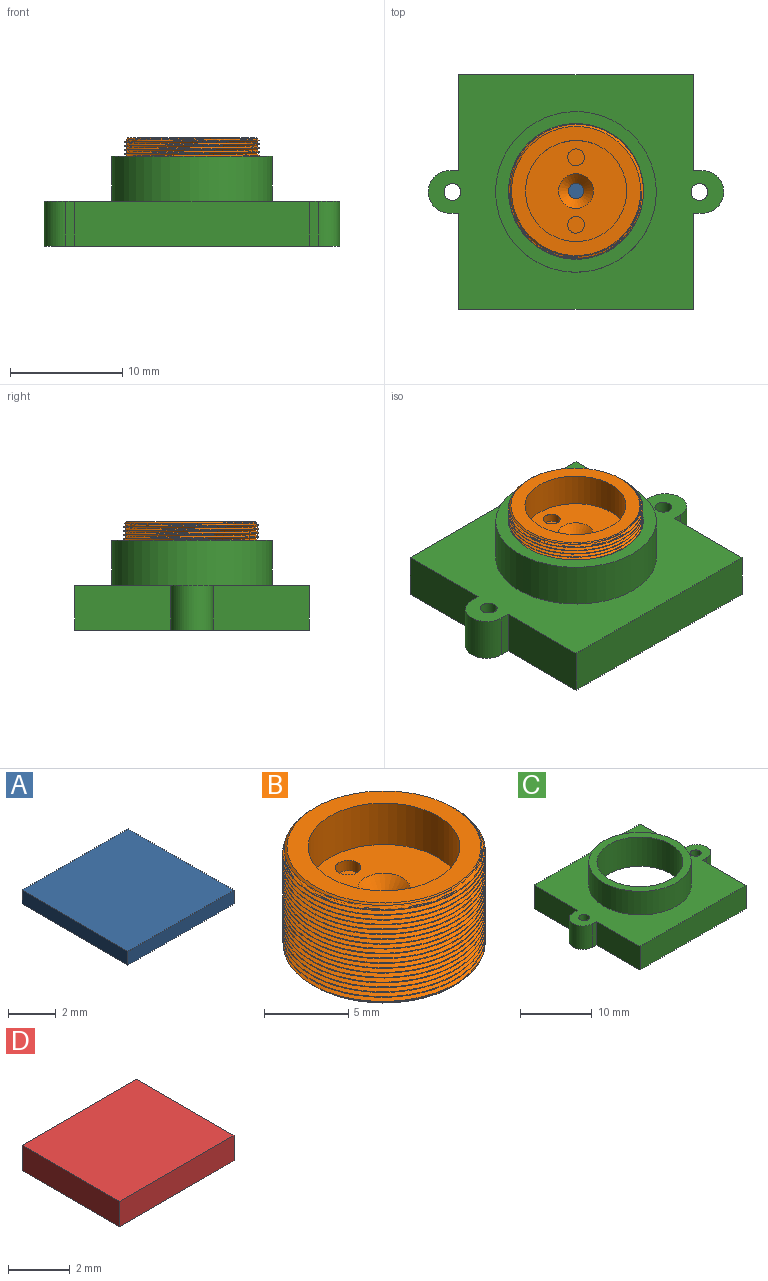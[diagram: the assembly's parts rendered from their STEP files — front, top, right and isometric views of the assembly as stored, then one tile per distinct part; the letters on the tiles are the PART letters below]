
ASSEMBLY  parts=4 mates=2
PART A: 6 faces, bbox 6.3x6.3x0.7 mm
  f0: plane 6.25x0.7mm, normal (0,-1,0), area 4.4mm2, adj f1,f3,f4,f5
  f1: plane 6.25x0.7mm, normal (1,0,0), area 4.4mm2, adj f0,f2,f4,f5
  f2: plane 6.25x0.7mm, normal (0,1,0), area 4.4mm2, adj f1,f3,f4,f5
  f3: plane 6.25x0.7mm, normal (-1,0,0), area 4.4mm2, adj f0,f2,f4,f5
  f4: plane 6.25x6.25mm, normal (0,0,1), area 39.1mm2, adj f0,f1,f2,f3
  f5: plane 6.25x6.25mm, normal (0,0,-1), area 39.1mm2, adj f0,f1,f2,f3
PART B: 21 faces, bbox 12x13.9x7.5 mm
  f0: plane 9x9mm, normal (0,0,1), area 52.5mm2, adj f2,f10,f17,f19
  f1: cylinder r=6mm len=12mm, axis (0,0,-1), area 27.8mm2, adj f11,f12,f15,f16
  f2: cylinder r=4.5mm len=9mm, axis (0,0,-1), area 84.8mm2, adj f0,f3
  f3: plane 11.5x11.5mm, normal (0,0,1), area 40.3mm2, adj f2,f13
  f4: cylinder r=4.5mm len=9mm, axis (0,0,1), area 35.3mm2, adj f5,f8
  f5: plane 11.5x11.5mm, normal (0,0,-1), area 40.2mm2, adj f4,f11,f15,f16
  f6: plane 6x6mm, normal (0,0,-1), area 26.8mm2, adj f7,f9
  f7: cylinder r=3mm len=6mm, axis (0,0,1), area 37.8mm2, adj f6,f8
  f8: plane 9x9mm, normal (0,0,-1), area 35.3mm2, adj f4,f7
  f9: cylinder r=0.69mm len=1.38mm, axis (0,0,1), area 0.6mm2, adj f6,f10
  f10: cone r=0.69mm half-angle=45deg, axis (0,0,1), area 8.6mm2, adj f0,f9
  f11: cone r=6mm half-angle=45deg, axis (0,0,1), area 7.2mm2, adj f1,f5,f15,f16
  f12: cone r=5.75mm half-angle=45deg, axis (0,0,-1), area 0.8mm2, adj f1,f13,f15,f16
  f13: cone r=5.75mm half-angle=45deg, axis (0,0,-1), area 6.7mm2, adj f3,f12,f14,f15
  f14: plane 0.11x0.08mm, normal (0,-1,0), area 0mm2, adj f13,f15,f16
  f15: bspline ~11.97x11.97mm, area 222.2mm2, adj f1,f5,f11,f12,f13,f14,f16
  f16: bspline ~13.86x12mm, area 220.7mm2, adj f1,f5,f11,f12,f14,f15
  f17: cylinder r=0.75mm len=1.5mm, axis (0,0,1), area 3.5mm2, adj f0,f18
  f18: plane 1.5x1.5mm, normal (0,0,1), area 1.8mm2, adj f17
  f19: cylinder r=0.75mm len=1.5mm, axis (0,0,1), area 3.5mm2, adj f0,f20
  f20: plane 1.5x1.5mm, normal (0,0,1), area 1.8mm2, adj f19
PART C: 24 faces, bbox 26.3x20.9x8 mm
  f0: plane 26.3x20.9mm, normal (0,0,-1), area 89.7mm2, adj f2,f3,f4,f5,f6,f7,f8,f9
  f1: cylinder r=6mm len=12mm, axis (0,0,1), area 188.5mm2, adj f18,f23
  f2: plane 8.55x4mm, normal (-1,0,0), area 34.2mm2, adj f0,f3,f14,f16
  f3: plane 20.9x4mm, normal (0,-1,0), area 83.6mm2, adj f0,f2,f4,f16
  f4: plane 8.55x4mm, normal (1,0,0), area 34.2mm2, adj f0,f3,f5,f16
  f5: plane 4x0.8mm, normal (0,-1,0), area 3.2mm2, adj f0,f4,f6,f16
  f6: cylinder r=1.9mm len=4mm, axis (0,0,-1), area 24mm2, adj f0,f5,f7,f16
  f7: plane 4x0.77mm, normal (-0.02,1,0), area 3.1mm2, adj f0,f6,f8,f16
  f8: plane 8.56x4mm, normal (1,0,0), area 34.3mm2, adj f0,f7,f9,f16
  f9: plane 20.9x4mm, normal (0,1,0), area 83.6mm2, adj f0,f8,f10,f16
  f10: plane 8.56x4mm, normal (-1,0,0), area 34.3mm2, adj f0,f9,f11,f16
  f11: plane 4x0.77mm, normal (0.02,1,0), area 3.1mm2, adj f0,f10,f12,f16
  f12: cylinder r=1.9mm len=4mm, axis (0,0,-1), area 24mm2, adj f0,f11,f14,f16
  f13: cylinder r=0.75mm len=4mm, axis (0,0,-1), area 18.8mm2, adj f0,f16
  f14: plane 4x0.8mm, normal (0,-1,0), area 3.2mm2, adj f0,f2,f12,f16
  f15: cylinder r=0.75mm len=4mm, axis (0,0,-1), area 18.8mm2, adj f0,f16
  f16: plane 26.3x20.9mm, normal (0,0,1), area 290.1mm2, adj f2,f3,f4,f5,f6,f7,f8,f9
  f17: cylinder r=7.15mm len=14.3mm, axis (0,0,-1), area 179.7mm2, adj f16,f18
  f18: plane 14.3x14.3mm, normal (0,0,1), area 47.5mm2, adj f1,f17
  f19: plane 19x3mm, normal (0,-1,0), area 57mm2, adj f0,f20,f22,f23
  f20: plane 19x3mm, normal (-1,0,0), area 57mm2, adj f0,f19,f21,f23
  f21: plane 19x3mm, normal (0,1,0), area 57mm2, adj f0,f20,f22,f23
  f22: plane 19x3mm, normal (1,0,0), area 57mm2, adj f0,f19,f21,f23
  f23: plane 19x19mm, normal (0,0,-1), area 247.9mm2, adj f1,f19,f20,f21,f22
PART D: 6 faces, bbox 5.2x4.5x1 mm
  f0: plane 5.24x1mm, normal (0,-1,0), area 5.2mm2, adj f1,f3,f4,f5
  f1: plane 4.46x1mm, normal (1,0,0), area 4.5mm2, adj f0,f2,f4,f5
  f2: plane 5.24x1mm, normal (0,1,0), area 5.2mm2, adj f1,f3,f4,f5
  f3: plane 4.46x1mm, normal (-1,0,0), area 4.5mm2, adj f0,f2,f4,f5
  f4: plane 5.24x4.46mm, normal (0,0,1), area 23.4mm2, adj f0,f1,f2,f3
  f5: plane 5.24x4.46mm, normal (0,0,-1), area 23.4mm2, adj f0,f1,f2,f3
PLACE A t=(0.05,-0.05,2.53)mm
PLACE B t=(-0.05,-0.01,5.23)mm
PLACE C t=(-0.05,-0.09,-0.43)mm
PLACE D t=(-0.03,0.05,-0.43)mm
MATE planar B.f4 <-> A.f4  axis (0,0,-1) through (-0.05,-0.01,3.23)mm
MATE planar D.f5 <-> C.f1  axis (0,0,-1) through (2.59,-2.18,-0.43)mm
